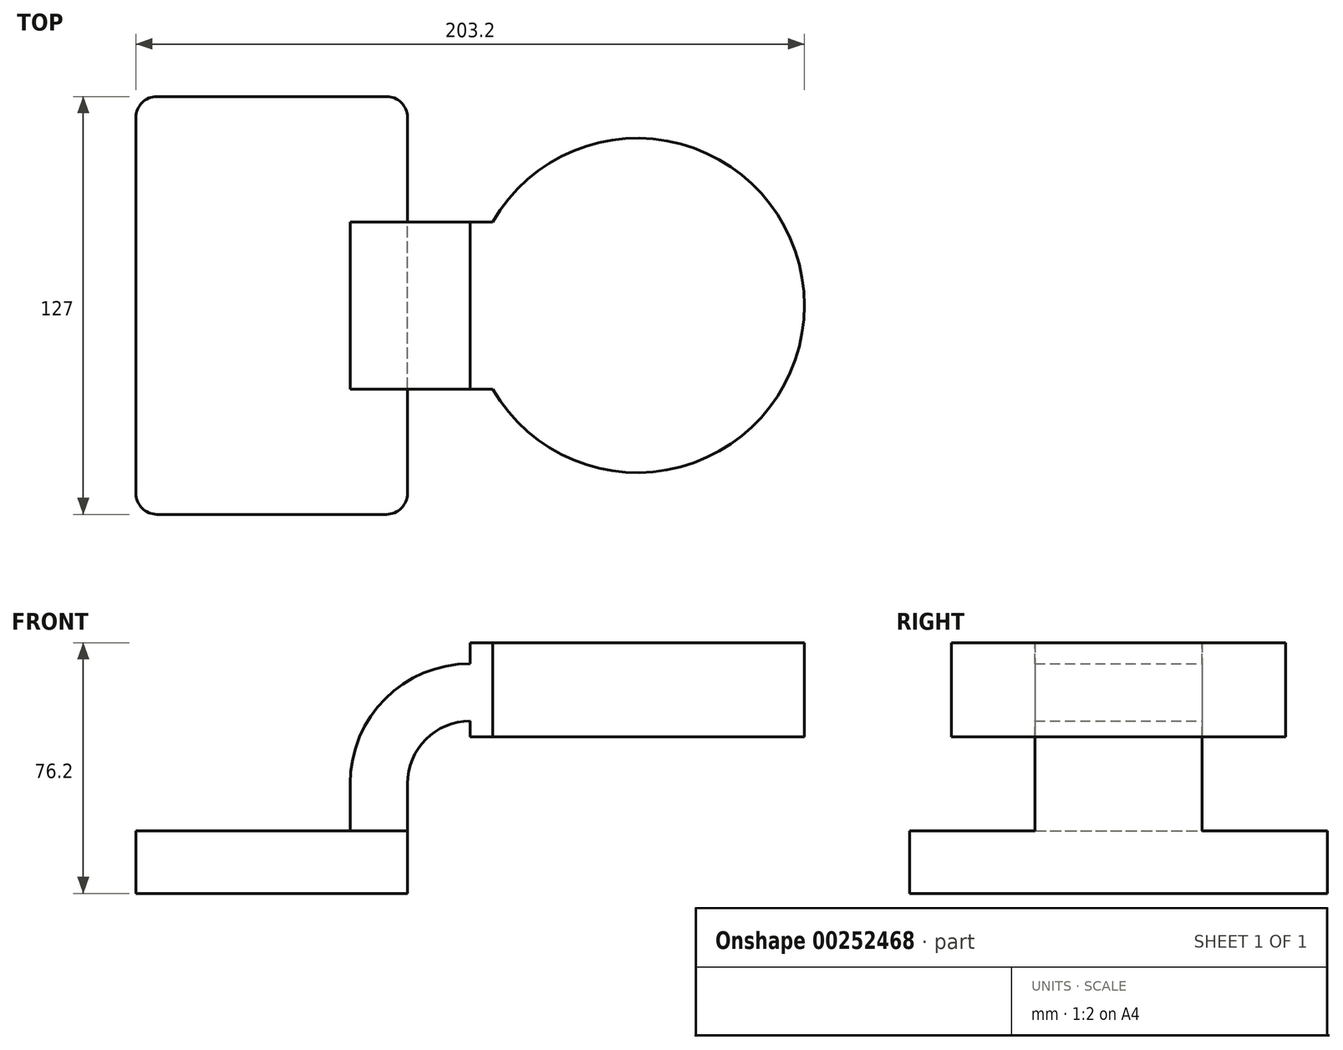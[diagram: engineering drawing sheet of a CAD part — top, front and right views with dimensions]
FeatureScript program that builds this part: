
annotation { "Feature Type Name" : "Feature", "Feature Type Description" : "" }
export const myFeature = defineFeature(function(context is Context, id is Id, definition is map)
    precondition{}
    {
        {
            var Q0;
            Q0=qCreatedBy(makeId("Front.planeOp"),FACE);
            var sketch = newSketch(context, id + "F0", { "sketchPlane" : qUnion([Q0])});
            skLineSegment(sketch, "E0.bottom", {"start": v(-41.28, 9.52) * mm, "end": v(41.28, 9.53) * mm});
            skLineSegment(sketch, "E0.top", {"start": v(-41.28, -9.53) * mm, "end": v(41.28, -9.53) * mm});
            skLineSegment(sketch, "E0.left", {"start": v(-41.28, 9.52) * mm, "end": v(-41.28, -9.53) * mm});
            skLineSegment(sketch, "E0.right", {"start": v(41.28, 9.53) * mm, "end": v(41.28, -9.52) * mm});
            skPoint(sketch, "E0.middle", {"position": v(0, 0) * mm});
            skLineSegment(sketch, "E1.bottom", {"start": v(111.12, 38.1) * mm, "end": v(60.32, 38.1) * mm});
            skLineSegment(sketch, "E1.top", {"start": v(111.12, 66.68) * mm, "end": v(60.32, 66.68) * mm});
            skLineSegment(sketch, "E1.left", {"start": v(111.13, 38.1) * mm, "end": v(111.12, 66.68) * mm});
            skLineSegment(sketch, "E1.right", {"start": v(60.32, 38.1) * mm, "end": v(60.32, 66.67) * mm});
            skPoint(sketch, "E1.middle", {"position": v(85.72, 52.39) * mm});
            skLineSegment(sketch, "E2", {"start": v(41.27, 9.53) * mm, "end": v(41.27, 23.83) * mm});
            skArc(sketch, "E3", {"start": v(41.28, 23.83) * mm, "mid": v(46.85, 37.3) * mm, "end": v(60.32, 42.88) * mm});
            skLineSegment(sketch, "E4", {"start": v(60.32, 42.88) * mm, "end": v(85.84, 42.88) * mm});
            skLineSegment(sketch, "E5.0", {"start": v(60.32, 60.3) * mm, "end": v(85.84, 60.3) * mm});
            skArc(sketch, "E5.1", {"start": v(23.85, 23.83) * mm, "mid": v(34.53, 49.62) * mm, "end": v(60.32, 60.3) * mm});
            skLineSegment(sketch, "E5.2", {"start": v(23.85, 9.53) * mm, "end": v(23.85, 23.83) * mm});
            skFitSpline(sketch, "E6", {"points": [v(-41.28, 9.52) * mm, v(60.32, 60.3) * mm], "startDerivative": vector(5.25, 89.48) * mm, "endDerivative": vector(149.58, -9.76) * mm});
            skSolve(sketch);
        }
        {
            var Q0;
            Q0=makeQuery(id+"F0.imprint","IMPRINT",FACE,{"disambiguationData":[TD([[makeQuery(id+"F0.imprint","IMPRINT",EDGE,{"derivedFrom":sQuery(id+"F0.wireOp",EDGE,"E0.top")}),1.0]])]});
            extrude(context, id + "F1", {"entities" : qUnion([Q0]), "endBound" : BoundingType.SYMMETRIC, "depth" : 127 * mm});
        }
        {
            var Q0;
            {var subQ1=sQuery(id+"F0.wireOp",EDGE,"E2");Q0=makeQuery(id+"F0.imprint","IMPRINT",FACE,{"disambiguationData":[TD([[makeQuery(id+"F0.imprint","IMPRINT",EDGE,{"derivedFrom":subQ1}),1.0]])]});}
            var Q1;
            {var subQ1=sQuery(id+"F0.wireOp",EDGE,"E1.bottom");Q1=makeQuery(id+"F0.imprint","IMPRINT",FACE,{"disambiguationData":[TD([[makeQuery(id+"F0.imprint","IMPRINT",EDGE,{"derivedFrom":subQ1}),-1.0]])]});}
            extrude(context, id + "F2", {"entities" : qUnion([Q0, Q1]), "operationType" : NewBodyOperationType.ADD, "endBound" : BoundingType.SYMMETRIC, "depth" : 50.8 * mm});
        }
        {
            var Q0;
            Q0=makeQuery(id+"F0.imprint","IMPRINT",FACE,{"disambiguationData":[TD([[makeQuery(id+"F0.imprint","IMPRINT",EDGE,{"derivedFrom":sQuery(id+"F0.wireOp",EDGE,"E5.1")}),1.0]])]});
            extrude(context, id + "F3", {"entities" : qUnion([Q0]), "operationType" : NewBodyOperationType.ADD, "endBound" : BoundingType.SYMMETRIC, "depth" : 15.88 * mm});
        }
        {
            var Q0;
            {var subQ1=sQuery(id+"F0.wireOp",EDGE,"E1.bottom");Q0=makeQuery(id+"F0.imprint","IMPRINT",FACE,{"disambiguationData":[TD([[makeQuery(id+"F0.imprint","IMPRINT",EDGE,{"derivedFrom":subQ1}),-1.0]])]});}
            var Q1;
            Q1=sQuery(id+"F0.wireOp",EDGE,"E1.left");
            revolve(context, id + "F4", {"operationType" : NewBodyOperationType.ADD, "entities" : qUnion([Q0]), "axis" : qUnion([Q1]), "revolveType" : RevolveType.FULL});
        }
        {
            var Q0;
            Q0=makeQuery(id+"F1.opExtrude","CAP_EDGE",EDGE,{"disambiguationData":[OSD([sQuery(id+"F0.wireOp",EDGE,"E0.right")])],"isStart":false});
            var Q1;
            Q1=makeQuery(id+"F1.opExtrude","CAP_EDGE",EDGE,{"disambiguationData":[OSD([sQuery(id+"F0.wireOp",EDGE,"E0.left")])],"isStart":false});
            var Q2;
            Q2=makeQuery(id+"F1.opExtrude","CAP_EDGE",EDGE,{"disambiguationData":[OSD([sQuery(id+"F0.wireOp",EDGE,"E0.right")])],"isStart":true});
            var Q3;
            Q3=makeQuery(id+"F1.opExtrude","CAP_EDGE",EDGE,{"disambiguationData":[OSD([sQuery(id+"F0.wireOp",EDGE,"E0.left")])],"isStart":true});
            fillet(context, id + "F5", {"entities" : qUnion([Q0, Q1, Q2, Q3]), "radius" : 6.35 * mm, "tangentPropagation" : true, "allowEdgeOverflow" : false});
        }
    });
